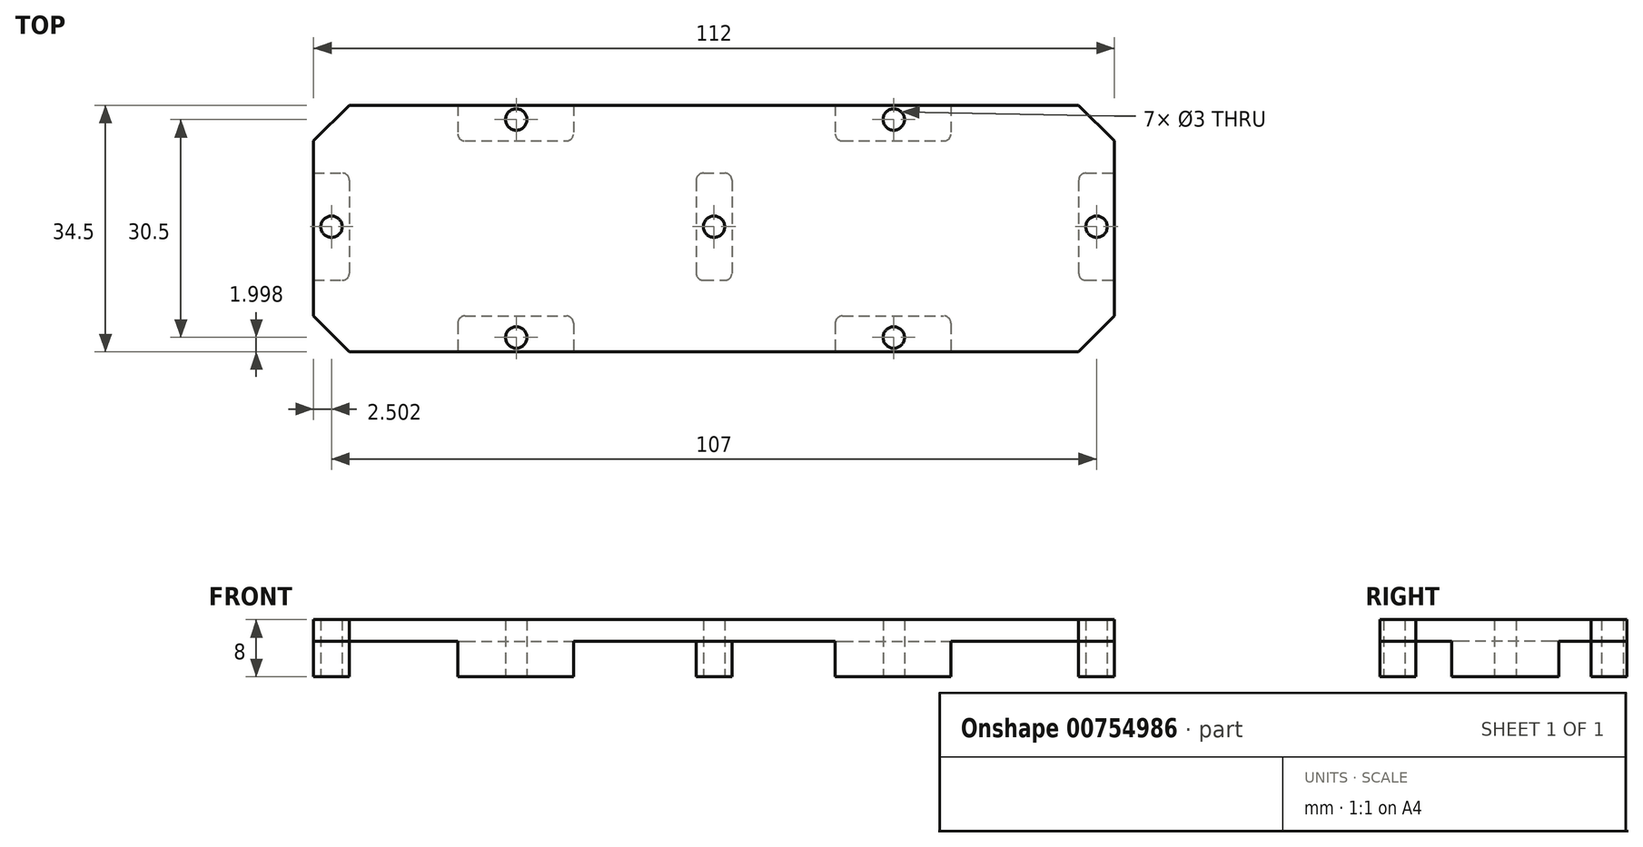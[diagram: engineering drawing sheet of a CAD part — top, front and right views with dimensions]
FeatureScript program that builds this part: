
annotation { "Feature Type Name" : "Feature", "Feature Type Description" : "" }
export const myFeature = defineFeature(function(context is Context, id is Id, definition is map)
    precondition{}
    {
        {
            var Q0;
            Q0=qCreatedBy(makeId("Top.planeOp"),FACE);
            var sketch = newSketch(context, id + "F0", { "sketchPlane" : qUnion([Q0])});
            skLineSegment(sketch, "E0.bottom", {"start": v(-67.6, 17.8) * mm, "end": v(-62.6, 17.8) * mm});
            skLineSegment(sketch, "E0.top", {"start": v(-67.6, 2.8) * mm, "end": v(-62.6, 2.8) * mm});
            skLineSegment(sketch, "E0.left", {"start": v(-67.6, 17.8) * mm, "end": v(-67.6, 2.8) * mm});
            skLineSegment(sketch, "E0.right", {"start": v(-62.6, 17.8) * mm, "end": v(-62.6, 2.8) * mm});
            skLineSegment(sketch, "E1.1.0.0", {"start": v(-14.1, 2.8) * mm, "end": v(-9.1, 2.8) * mm});
            skLineSegment(sketch, "E1.1.0.1", {"start": v(-14.1, 17.8) * mm, "end": v(-14.1, 2.8) * mm});
            skLineSegment(sketch, "E1.1.0.2", {"start": v(-9.1, 17.8) * mm, "end": v(-9.1, 2.8) * mm});
            skLineSegment(sketch, "E1.1.0.3", {"start": v(-14.1, 17.8) * mm, "end": v(-9.1, 17.8) * mm});
            skLineSegment(sketch, "E1.2.0.0", {"start": v(39.4, 2.8) * mm, "end": v(44.4, 2.8) * mm});
            skLineSegment(sketch, "E1.2.0.1", {"start": v(39.4, 17.8) * mm, "end": v(39.4, 2.8) * mm});
            skLineSegment(sketch, "E1.2.0.2", {"start": v(44.4, 17.8) * mm, "end": v(44.4, 2.8) * mm});
            skLineSegment(sketch, "E1.2.0.3", {"start": v(39.4, 17.8) * mm, "end": v(44.4, 17.8) * mm});
            skLineSegment(sketch, "E1.direction1", {"start": v(-67.6, 2.8) * mm, "end": v(-14.1, 2.8) * mm, "construction": true});
            skLineSegment(sketch, "E2.bottom", {"start": v(-47.44, 27.3) * mm, "end": v(-31.26, 27.3) * mm});
            skLineSegment(sketch, "E2.top", {"start": v(-47.44, 22.3) * mm, "end": v(-31.26, 22.3) * mm});
            skLineSegment(sketch, "E2.left", {"start": v(-47.44, 27.3) * mm, "end": v(-47.44, 22.3) * mm});
            skLineSegment(sketch, "E2.right", {"start": v(-31.26, 27.3) * mm, "end": v(-31.26, 22.3) * mm});
            skLineSegment(sketch, "E3.0.1.0", {"start": v(-47.44, -2.2) * mm, "end": v(-31.26, -2.2) * mm});
            skLineSegment(sketch, "E3.0.1.1", {"start": v(-47.44, -7.2) * mm, "end": v(-31.26, -7.2) * mm});
            skLineSegment(sketch, "E3.0.1.2", {"start": v(-31.26, -2.2) * mm, "end": v(-31.26, -7.2) * mm});
            skLineSegment(sketch, "E3.0.1.3", {"start": v(-47.44, -2.2) * mm, "end": v(-47.44, -7.2) * mm});
            skLineSegment(sketch, "E3.1.0.0", {"start": v(5.36, 27.3) * mm, "end": v(21.54, 27.3) * mm});
            skLineSegment(sketch, "E3.1.0.1", {"start": v(5.36, 22.3) * mm, "end": v(21.54, 22.3) * mm});
            skLineSegment(sketch, "E3.1.0.2", {"start": v(21.54, 27.3) * mm, "end": v(21.54, 22.3) * mm});
            skLineSegment(sketch, "E3.1.0.3", {"start": v(5.36, 27.3) * mm, "end": v(5.36, 22.3) * mm});
            skLineSegment(sketch, "E3.1.1.0", {"start": v(5.36, -2.2) * mm, "end": v(21.54, -2.2) * mm});
            skLineSegment(sketch, "E3.1.1.1", {"start": v(5.36, -7.2) * mm, "end": v(21.54, -7.2) * mm});
            skLineSegment(sketch, "E3.1.1.2", {"start": v(21.54, -2.2) * mm, "end": v(21.54, -7.2) * mm});
            skLineSegment(sketch, "E3.1.1.3", {"start": v(5.36, -2.2) * mm, "end": v(5.36, -7.2) * mm});
            skLineSegment(sketch, "E3.direction1", {"start": v(-47.44, 22.3) * mm, "end": v(5.36, 22.3) * mm, "construction": true});
            skLineSegment(sketch, "E3.direction2", {"start": v(-47.44, 22.3) * mm, "end": v(-47.44, -7.2) * mm, "construction": true});
            skSolve(sketch);
        }
        {
            var Q0;
            Q0=qCreatedBy(makeId("Top.planeOp"),FACE);
            var sketch = newSketch(context, id + "F1", { "sketchPlane" : qUnion([Q0])});
            skLineSegment(sketch, "E4.bottom", {"start": v(-67.6, 27.3) * mm, "end": v(44.4, 27.3) * mm});
            skLineSegment(sketch, "E4.top", {"start": v(-67.6, -7.2) * mm, "end": v(44.4, -7.2) * mm});
            skLineSegment(sketch, "E4.left", {"start": v(-67.6, 27.3) * mm, "end": v(-67.6, -7.2) * mm});
            skLineSegment(sketch, "E4.right", {"start": v(44.4, 27.3) * mm, "end": v(44.4, -7.2) * mm});
            skSolve(sketch);
        }
        {
            var Q0;
            Q0 = qSketchRegion(id + "F1", true);
            extrude(context, id + "F2", {"entities" : qUnion([Q0]), "depth" : 3 * mm, "offsetDistance" : 25 * mm});
        }
        {
            var Q0;
            Q0 = qSketchRegion(id + "F0", true);
            extrude(context, id + "F3", {"entities" : qUnion([Q0]), "operationType" : NewBodyOperationType.ADD, "oppositeDirection" : true, "depth" : 5 * mm, "offsetDistance" : 25 * mm});
        }
        {
            var Q0;
            Q0=makeQuery(id+"F3.opExtrude","CAP_FACE",FACE,{"disambiguationData":[OSD([sQuery(id+"F0.wireOp",EDGE,"E1.1.0.0"),sQuery(id+"F0.wireOp",EDGE,"E1.1.0.1"),sQuery(id+"F0.wireOp",EDGE,"E1.1.0.2"),sQuery(id+"F0.wireOp",EDGE,"E1.1.0.3")])],"isStart":false});
            var sketch = newSketch(context, id + "F4", { "sketchPlane" : qUnion([Q0])});
            skCircle(sketch, "E5", {"center": v(-65.1, -10.3) * mm, "radius": 1.5 * mm});
            skCircle(sketch, "E6", {"center": v(-11.6, -10.3) * mm, "radius": 1.5 * mm});
            skCircle(sketch, "E7", {"center": v(41.9, -10.3) * mm, "radius": 1.5 * mm});
            skCircle(sketch, "E8", {"center": v(-39.26, 5.2) * mm, "radius": 1.5 * mm});
            skCircle(sketch, "E9", {"center": v(13.54, 5.2) * mm, "radius": 1.5 * mm});
            skCircle(sketch, "E10", {"center": v(13.54, -25.3) * mm, "radius": 1.5 * mm});
            skCircle(sketch, "E11", {"center": v(-39.26, -25.3) * mm, "radius": 1.5 * mm});
            skSolve(sketch);
        }
        {
            var Q0;
            Q0 = qSketchRegion(id + "F4", true);
            extrude(context, id + "F5", {"entities" : qUnion([Q0]), "operationType" : NewBodyOperationType.REMOVE, "oppositeDirection" : true, "depth" : 25 * mm, "offsetDistance" : 25 * mm});
        }
        {
            var Q0;
            Q0=makeQuery(id+"F3.opExtrude","SWEPT_EDGE",EDGE,{"disambiguationData":[OSD([sQuery(id+"F0.wireOp",EDGE,"E0.top"),sQuery(id+"F0.wireOp",EDGE,"E0.right")])]});
            var Q1;
            Q1=makeQuery(id+"F3.opExtrude","SWEPT_EDGE",EDGE,{"disambiguationData":[OSD([sQuery(id+"F0.wireOp",EDGE,"E0.bottom"),sQuery(id+"F0.wireOp",EDGE,"E0.right")])]});
            var Q2;
            Q2=makeQuery(id+"F3.opExtrude","SWEPT_EDGE",EDGE,{"disambiguationData":[OSD([sQuery(id+"F0.wireOp",EDGE,"E3.0.1.0"),sQuery(id+"F0.wireOp",EDGE,"E3.0.1.3")])]});
            var Q3;
            Q3=makeQuery(id+"F3.opExtrude","SWEPT_EDGE",EDGE,{"disambiguationData":[OSD([sQuery(id+"F0.wireOp",EDGE,"E3.0.1.0"),sQuery(id+"F0.wireOp",EDGE,"E3.0.1.2")])]});
            var Q4;
            Q4=makeQuery(id+"F3.opExtrude","SWEPT_EDGE",EDGE,{"disambiguationData":[OSD([sQuery(id+"F0.wireOp",EDGE,"E2.top"),sQuery(id+"F0.wireOp",EDGE,"E2.left")])]});
            var Q5;
            Q5=makeQuery(id+"F3.opExtrude","SWEPT_EDGE",EDGE,{"disambiguationData":[OSD([sQuery(id+"F0.wireOp",EDGE,"E2.top"),sQuery(id+"F0.wireOp",EDGE,"E2.right")])]});
            var Q6;
            Q6=makeQuery(id+"F3.opExtrude","SWEPT_EDGE",EDGE,{"disambiguationData":[OSD([sQuery(id+"F0.wireOp",EDGE,"E1.1.0.1"),sQuery(id+"F0.wireOp",EDGE,"E1.1.0.3")])]});
            var Q7;
            Q7=makeQuery(id+"F3.opExtrude","SWEPT_EDGE",EDGE,{"disambiguationData":[OSD([sQuery(id+"F0.wireOp",EDGE,"E1.1.0.0"),sQuery(id+"F0.wireOp",EDGE,"E1.1.0.1")])]});
            var Q8;
            Q8=makeQuery(id+"F3.opExtrude","SWEPT_EDGE",EDGE,{"disambiguationData":[OSD([sQuery(id+"F0.wireOp",EDGE,"E3.1.1.0"),sQuery(id+"F0.wireOp",EDGE,"E3.1.1.3")])]});
            var Q9;
            Q9=makeQuery(id+"F3.opExtrude","SWEPT_EDGE",EDGE,{"disambiguationData":[OSD([sQuery(id+"F0.wireOp",EDGE,"E3.1.1.0"),sQuery(id+"F0.wireOp",EDGE,"E3.1.1.2")])]});
            var Q10;
            Q10=makeQuery(id+"F3.opExtrude","SWEPT_EDGE",EDGE,{"disambiguationData":[OSD([sQuery(id+"F0.wireOp",EDGE,"E1.2.0.0"),sQuery(id+"F0.wireOp",EDGE,"E1.2.0.1")])]});
            var Q11;
            Q11=makeQuery(id+"F3.opExtrude","SWEPT_EDGE",EDGE,{"disambiguationData":[OSD([sQuery(id+"F0.wireOp",EDGE,"E1.1.0.0"),sQuery(id+"F0.wireOp",EDGE,"E1.1.0.2")])]});
            var Q12;
            Q12=makeQuery(id+"F3.opExtrude","SWEPT_EDGE",EDGE,{"disambiguationData":[OSD([sQuery(id+"F0.wireOp",EDGE,"E1.1.0.2"),sQuery(id+"F0.wireOp",EDGE,"E1.1.0.3")])]});
            var Q13;
            Q13=makeQuery(id+"F3.opExtrude","SWEPT_EDGE",EDGE,{"disambiguationData":[OSD([sQuery(id+"F0.wireOp",EDGE,"E1.2.0.1"),sQuery(id+"F0.wireOp",EDGE,"E1.2.0.3")])]});
            var Q14;
            Q14=makeQuery(id+"F3.opExtrude","SWEPT_EDGE",EDGE,{"disambiguationData":[OSD([sQuery(id+"F0.wireOp",EDGE,"E3.1.0.1"),sQuery(id+"F0.wireOp",EDGE,"E3.1.0.2")])]});
            var Q15;
            Q15=makeQuery(id+"F3.opExtrude","SWEPT_EDGE",EDGE,{"disambiguationData":[OSD([sQuery(id+"F0.wireOp",EDGE,"E3.1.0.1"),sQuery(id+"F0.wireOp",EDGE,"E3.1.0.3")])]});
            fillet(context, id + "F6", {"entities" : qUnion([Q0, Q1, Q2, Q3, Q4, Q5, Q6, Q7, Q8, Q9, Q10, Q11, Q12, Q13, Q14, Q15]), "radius" : 1 * mm, "tangentPropagation" : true, "allowEdgeOverflow" : false});
        }
        {
            var Q0;
            Q0=makeQuery(id+"F2.opExtrude","SWEPT_EDGE",EDGE,{"disambiguationData":[OSD([sQuery(id+"F1.wireOp",EDGE,"E4.bottom"),sQuery(id+"F1.wireOp",EDGE,"E4.left")])]});
            var Q1;
            Q1=makeQuery(id+"F2.opExtrude","SWEPT_EDGE",EDGE,{"disambiguationData":[OSD([sQuery(id+"F1.wireOp",EDGE,"E4.bottom"),sQuery(id+"F1.wireOp",EDGE,"E4.right")])]});
            var Q2;
            Q2=makeQuery(id+"F2.opExtrude","SWEPT_EDGE",EDGE,{"disambiguationData":[OSD([sQuery(id+"F1.wireOp",EDGE,"E4.top"),sQuery(id+"F1.wireOp",EDGE,"E4.right")])]});
            var Q3;
            Q3=makeQuery(id+"F2.opExtrude","SWEPT_EDGE",EDGE,{"disambiguationData":[OSD([sQuery(id+"F1.wireOp",EDGE,"E4.top"),sQuery(id+"F1.wireOp",EDGE,"E4.left")])]});
            chamfer(context, id + "F7", {"entities" : qUnion([Q0, Q1, Q2, Q3]), "width" : 5 * mm, "tangentPropagation" : true});
        }
    });
